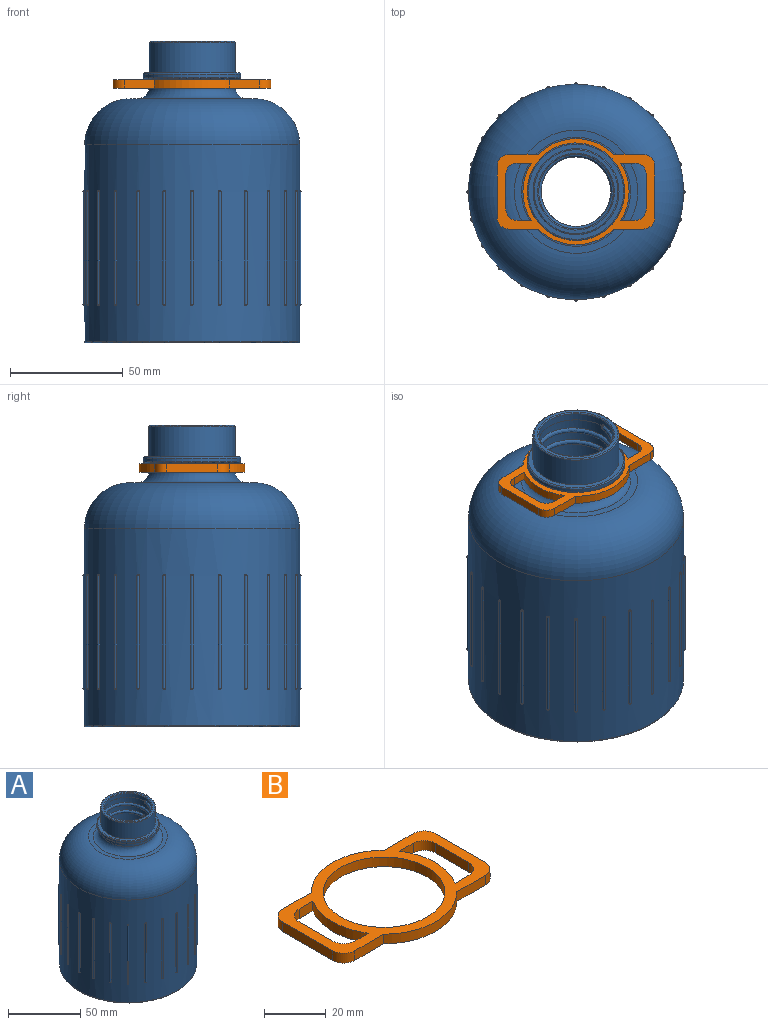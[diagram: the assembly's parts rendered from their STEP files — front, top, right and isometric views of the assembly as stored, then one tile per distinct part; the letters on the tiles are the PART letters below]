
ASSEMBLY  parts=2 mates=1
PART A: 166 faces, bbox 103.6x109.9x133.9 mm
  f0: cylinder r=47.62mm len=95.25mm, axis (0,0,1), area 24527mm2, adj f13,f29,f46,f47,f48,f49,f50,f51
  f1: cylinder r=16.51mm len=33.02mm, axis (0,0,1), area 332.1mm2, adj f3,f38,f39,f40,f43
  f2: cylinder r=16.52mm len=33.05mm, axis (0,0,1), area 865.6mm2, adj f3,f36,f37,f38,f39,f40,f41
  f3: plane 33.05x33.05mm, normal (0,0,-1), area 1.1mm2, adj f1,f2,f38,f39
  f4: cylinder r=16.51mm len=33.02mm, axis (0,0,1), area 780mm2, adj f31,f36,f37,f39,f41
  f5: plane 87.63x87.63mm, normal (0,0,1), area 679mm2, adj f10,f32
  f6: cylinder r=19.05mm len=38.1mm, axis (0,0,-1), area 456mm2, adj f30,f35
  f7: cylinder r=45.09mm len=90.17mm, axis (0,0,-1), area 945.5mm2, adj f8,f23,f25,f26,f28
  f8: plane 90.17x90.17mm, normal (0,0,-1), area 2.8mm2, adj f7,f22,f23,f25
  f9: plane 83.82x83.82mm, normal (0,0,-1), area 165.9mm2, adj f10,f18
  f10: cylinder r=41.27mm len=82.55mm, axis (0,0,1), area 16964.1mm2, adj f5,f9
  f11: plane 94.23x94.23mm, normal (0,0,-1), area 443.9mm2, adj f28,f29
  f12: plane 54.61x54.61mm, normal (0,0,1), area 513mm2, adj f13,f30
  f13: torus R=27.3mm, axis (0,0,1), area 8070.4mm2, adj f0,f12
  f14: cylinder r=19.05mm len=38.1mm, axis (0,0,-1), area 1611.3mm2, adj f34,f42
  f15: plane 37.08x37.08mm, normal (0,0,1), area 170.3mm2, adj f42,f43
  f16: plane 90.17x90.17mm, normal (0,0,-1), area 178.6mm2, adj f17,f19
  f17: cylinder r=45.09mm len=90.17mm, axis (0,0,-1), area 1089.4mm2, adj f16,f21,f24,f25,f27
  f18: cylinder r=41.91mm len=83.82mm, axis (0,0,-1), area 535.1mm2, adj f9,f20
  f19: cylinder r=44.45mm len=88.9mm, axis (0,0,-1), area 567.5mm2, adj f16,f20
  f20: plane 88.9x88.9mm, normal (0,0,-1), area 689.1mm2, adj f18,f19
  f21: plane 90.17x90.17mm, normal (0,0,1), area 2.8mm2, adj f17,f22,f24,f25
  f22: cylinder r=45.07mm len=90.14mm, axis (0,0,-1), area 1347.5mm2, adj f8,f21,f23,f24,f25,f26,f27
  f23: plane 0.25x0.14mm, normal (0,1,0), area 0mm2, adj f7,f8,f22,f26
  f24: plane 0.25x0.14mm, normal (0,1,0), area 0mm2, adj f17,f21,f22,f27
  f25: bspline ~109.4x94.74mm, area 1485mm2, adj f7,f8,f17,f21,f22,f26,f27
  f26: bspline ~2.31x1.44mm, area 3.9mm2, adj f7,f22,f23,f25
  f27: bspline ~2.31x1.44mm, area 3.9mm2, adj f17,f22,f24,f25
  f28: torus R=45.59mm, axis (0,0,1), area 227mm2, adj f7,f11
  f29: torus R=47.12mm, axis (0,0,1), area 237.9mm2, adj f0,f11
  f30: torus R=24.13mm, axis (0,0,1), area 1047.7mm2, adj f6,f12
  f31: torus R=21.59mm, axis (0,0,-1), area 904.7mm2, adj f4,f32
  f32: torus R=20.96mm, axis (0,0,1), area 7942.1mm2, adj f5,f31
  f33: cylinder r=21.59mm len=43.18mm, axis (0,0,-1), area 206.7mm2, adj f44,f45
  f34: plane 42.16x42.16mm, normal (0,0,1), area 256.2mm2, adj f14,f45
  f35: plane 42.16x42.16mm, normal (0,0,-1), area 256.2mm2, adj f6,f44
  f36: plane 33.05x33.05mm, normal (0,0,1), area 1.1mm2, adj f2,f4,f37,f39
  f37: plane 0.25x0.17mm, normal (0,-1,0), area 0mm2, adj f2,f4,f36,f41
  f38: plane 0.25x0.17mm, normal (0,1,0), area 0mm2, adj f1,f2,f3,f40
  f39: bspline ~33.04x33.01mm, area 710.9mm2, adj f1,f2,f3,f4,f36,f40,f41
  f40: bspline ~2.35x1.67mm, area 4mm2, adj f1,f2,f38,f39
  f41: bspline ~2.35x1.67mm, area 4mm2, adj f2,f4,f37,f39
  f42: torus R=18.54mm, axis (0,0,1), area 94.6mm2, adj f14,f15
  f43: torus R=17.02mm, axis (0,0,1), area 83.7mm2, adj f1,f15
  f44: torus R=21.08mm, axis (0,0,1), area 107.3mm2, adj f33,f35
  f45: torus R=21.08mm, axis (0,0,1), area 107.3mm2, adj f33,f34
  f46: cylinder r=0.64mm len=49.78mm, axis (0,0,-1), area 99.7mm2, adj f0,f141,f165
  f47: plane 0.25x0.13mm, normal (0,0,1), area 0mm2, adj f0,f165
  f48: plane 0.25x0.13mm, normal (0,0,-1), area 0mm2, adj f0,f141
  f49: cylinder r=0.64mm len=49.78mm, axis (0,0,-1), area 99.7mm2, adj f0,f140,f164
  f50: plane 0.25x0.16mm, normal (0,0,1), area 0mm2, adj f0,f164
  f51: plane 0.25x0.16mm, normal (0,0,-1), area 0mm2, adj f0,f140
  f52: cylinder r=0.64mm len=49.78mm, axis (0,0,-1), area 99.7mm2, adj f0,f139,f163
  f53: plane 0.24x0.19mm, normal (0,0,1), area 0mm2, adj f0,f163
  f54: plane 0.24x0.19mm, normal (0,0,-1), area 0mm2, adj f0,f139
  f55: cylinder r=0.64mm len=49.78mm, axis (0,0,-1), area 99.7mm2, adj f0,f138,f162
  f56: plane 0.22x0.22mm, normal (0,0,1), area 0mm2, adj f0,f162
  f57: plane 0.22x0.22mm, normal (0,0,-1), area 0mm2, adj f0,f138
  f58: cylinder r=0.64mm len=49.78mm, axis (0,0,-1), area 99.7mm2, adj f0,f137,f161
  f59: plane 0.24x0.19mm, normal (0,0,1), area 0mm2, adj f0,f161
  f60: plane 0.24x0.19mm, normal (0,0,-1), area 0mm2, adj f0,f137
  f61: cylinder r=0.64mm len=49.78mm, axis (0,0,-1), area 99.7mm2, adj f0,f136,f160
  f62: plane 0.25x0.16mm, normal (0,0,1), area 0mm2, adj f0,f160
  f63: plane 0.25x0.16mm, normal (0,0,-1), area 0mm2, adj f0,f136
  f64: cylinder r=0.64mm len=49.78mm, axis (0,0,-1), area 99.7mm2, adj f0,f135,f159
  f65: plane 0.25x0.13mm, normal (0,0,1), area 0mm2, adj f0,f159
  f66: plane 0.76x0.64mm, normal (0,0,-1), area 0mm2, adj f0,f135
  f67: cylinder r=0.64mm len=49.78mm, axis (0,0,-1), area 99.7mm2, adj f0,f134,f158
  f68: plane 0.25x0.16mm, normal (0,0,1), area 0mm2, adj f0,f158
  f69: plane 0.25x0.16mm, normal (0,0,-1), area 0mm2, adj f0,f134
  f70: cylinder r=0.64mm len=49.78mm, axis (0,0,-1), area 99.7mm2, adj f0,f133,f157
  f71: plane 0.24x0.19mm, normal (0,0,1), area 0mm2, adj f0,f157
  f72: plane 0.24x0.19mm, normal (0,0,-1), area 0mm2, adj f0,f133
  f73: cylinder r=0.64mm len=49.78mm, axis (0,0,-1), area 99.7mm2, adj f0,f132,f156
  f74: plane 0.22x0.22mm, normal (0,0,1), area 0mm2, adj f0,f156
  f75: plane 0.22x0.22mm, normal (0,0,-1), area 0mm2, adj f0,f132
  f76: cylinder r=0.64mm len=49.78mm, axis (0,0,-1), area 99.7mm2, adj f0,f131,f155
  f77: plane 0.24x0.19mm, normal (0,0,1), area 0mm2, adj f0,f155
  f78: plane 0.24x0.19mm, normal (0,0,-1), area 0mm2, adj f0,f131
  f79: cylinder r=0.64mm len=49.78mm, axis (0,0,-1), area 99.7mm2, adj f0,f130,f154
  f80: plane 0.25x0.16mm, normal (0,0,1), area 0mm2, adj f0,f154
  f81: plane 0.25x0.16mm, normal (0,0,-1), area 0mm2, adj f0,f130
  f82: cylinder r=0.64mm len=49.78mm, axis (0,0,-1), area 99.7mm2, adj f0,f129,f153
  f83: plane 0.25x0.13mm, normal (0,0,1), area 0mm2, adj f0,f153
  f84: plane 0.25x0.13mm, normal (0,0,-1), area 0mm2, adj f0,f129
  f85: cylinder r=0.64mm len=49.78mm, axis (0,0,-1), area 99.7mm2, adj f0,f128,f152
  f86: plane 0.25x0.16mm, normal (0,0,1), area 0mm2, adj f0,f152
  f87: plane 0.25x0.16mm, normal (0,0,-1), area 0mm2, adj f0,f128
  f88: cylinder r=0.64mm len=49.78mm, axis (0,0,-1), area 99.7mm2, adj f0,f127,f151
  f89: plane 0.24x0.19mm, normal (0,0,1), area 0mm2, adj f0,f151
  f90: plane 0.24x0.19mm, normal (0,0,-1), area 0mm2, adj f0,f127
  f91: cylinder r=0.64mm len=49.78mm, axis (0,0,-1), area 99.7mm2, adj f0,f126,f150
  f92: plane 0.22x0.22mm, normal (0,0,1), area 0mm2, adj f0,f150
  f93: plane 0.22x0.22mm, normal (0,0,-1), area 0mm2, adj f0,f126
  f94: cylinder r=0.64mm len=49.78mm, axis (0,0,-1), area 99.7mm2, adj f0,f125,f149
  f95: plane 0.24x0.19mm, normal (0,0,1), area 0mm2, adj f0,f149
  f96: plane 0.24x0.19mm, normal (0,0,-1), area 0mm2, adj f0,f125
  f97: cylinder r=0.64mm len=49.78mm, axis (0,0,-1), area 99.7mm2, adj f0,f124,f148
  f98: plane 0.25x0.16mm, normal (0,0,1), area 0mm2, adj f0,f148
  f99: plane 0.25x0.16mm, normal (0,0,-1), area 0mm2, adj f0,f124
  f100: cylinder r=0.64mm len=49.78mm, axis (0,0,-1), area 99.7mm2, adj f0,f123,f147
  f101: plane 0.25x0.13mm, normal (0,0,1), area 0mm2, adj f0,f147
  f102: plane 0.76x0.64mm, normal (0,0,-1), area 0mm2, adj f0,f123
  f103: cylinder r=0.64mm len=49.78mm, axis (0,0,-1), area 99.7mm2, adj f0,f122,f146
  f104: plane 0.25x0.16mm, normal (0,0,1), area 0mm2, adj f0,f146
  f105: plane 0.25x0.16mm, normal (0,0,-1), area 0mm2, adj f0,f122
  f106: cylinder r=0.64mm len=49.78mm, axis (0,0,-1), area 99.7mm2, adj f0,f121,f145
  f107: plane 0.24x0.19mm, normal (0,0,1), area 0mm2, adj f0,f145
  f108: plane 0.24x0.19mm, normal (0,0,-1), area 0mm2, adj f0,f121
  f109: cylinder r=0.64mm len=49.78mm, axis (0,0,-1), area 99.7mm2, adj f0,f120,f144
  f110: plane 0.22x0.22mm, normal (0,0,1), area 0mm2, adj f0,f144
  f111: plane 0.22x0.22mm, normal (0,0,-1), area 0mm2, adj f0,f120
  f112: cylinder r=0.64mm len=49.78mm, axis (0,0,-1), area 99.7mm2, adj f0,f119,f143
  f113: plane 0.24x0.19mm, normal (0,0,1), area 0mm2, adj f0,f143
  f114: plane 0.24x0.19mm, normal (0,0,-1), area 0mm2, adj f0,f119
  f115: cylinder r=0.64mm len=49.78mm, axis (0,0,-1), area 99.7mm2, adj f0,f118,f142
  f116: plane 0.25x0.16mm, normal (0,0,1), area 0mm2, adj f0,f142
  f117: plane 0.25x0.16mm, normal (0,0,-1), area 0mm2, adj f0,f118
  f118: torus R=0.13mm, axis (0,0,-1), area 1.1mm2, adj f0,f115,f117
  f119: torus R=0.13mm, axis (0,0,-1), area 1.1mm2, adj f0,f112,f114
  f120: torus R=0.13mm, axis (0,0,-1), area 1.1mm2, adj f0,f109,f111
  f121: torus R=0.13mm, axis (0,0,-1), area 1.1mm2, adj f0,f106,f108
  f122: torus R=0.13mm, axis (0,0,-1), area 1.1mm2, adj f0,f103,f105
  f123: torus R=0.13mm, axis (0,0,-1), area 1.6mm2, adj f0,f100,f102
  f124: torus R=0.13mm, axis (0,0,-1), area 1.1mm2, adj f0,f97,f99
  f125: torus R=0.13mm, axis (0,0,-1), area 1.1mm2, adj f0,f94,f96
  f126: torus R=0.13mm, axis (0,0,-1), area 1.1mm2, adj f0,f91,f93
  f127: torus R=0.13mm, axis (0,0,-1), area 1.1mm2, adj f0,f88,f90
  f128: torus R=0.13mm, axis (0,0,-1), area 1.1mm2, adj f0,f85,f87
  f129: torus R=0.13mm, axis (0,0,-1), area 1.1mm2, adj f0,f82,f84
  f130: torus R=0.13mm, axis (0,0,-1), area 1.1mm2, adj f0,f79,f81
  f131: torus R=0.13mm, axis (0,0,-1), area 1.1mm2, adj f0,f76,f78
  f132: torus R=0.13mm, axis (0,0,-1), area 1.1mm2, adj f0,f73,f75
  f133: torus R=0.13mm, axis (0,0,-1), area 1.1mm2, adj f0,f70,f72
  f134: torus R=0.13mm, axis (0,0,-1), area 1.1mm2, adj f0,f67,f69
  f135: torus R=0.13mm, axis (0,0,-1), area 0.7mm2, adj f0,f64,f66
  f136: torus R=0.13mm, axis (0,0,-1), area 1.1mm2, adj f0,f61,f63
  f137: torus R=0.13mm, axis (0,0,-1), area 1.1mm2, adj f0,f58,f60
  f138: torus R=0.13mm, axis (0,0,-1), area 1.1mm2, adj f0,f55,f57
  f139: torus R=0.13mm, axis (0,0,-1), area 1.1mm2, adj f0,f52,f54
  f140: torus R=0.13mm, axis (0,0,-1), area 1.1mm2, adj f0,f49,f51
  f141: torus R=0.13mm, axis (0,0,-1), area 1.1mm2, adj f0,f46,f48
  f142: torus R=0.13mm, axis (0,0,-1), area 1.1mm2, adj f0,f115,f116
  f143: torus R=0.13mm, axis (0,0,-1), area 1.1mm2, adj f0,f112,f113
  f144: torus R=0.13mm, axis (0,0,-1), area 1.1mm2, adj f0,f109,f110
  f145: torus R=0.13mm, axis (0,0,-1), area 1.1mm2, adj f0,f106,f107
  f146: torus R=0.13mm, axis (0,0,-1), area 1.1mm2, adj f0,f103,f104
  f147: torus R=0.13mm, axis (0,0,-1), area 1.1mm2, adj f0,f100,f101
  f148: torus R=0.13mm, axis (0,0,-1), area 1.1mm2, adj f0,f97,f98
  f149: torus R=0.13mm, axis (0,0,-1), area 1.1mm2, adj f0,f94,f95
  f150: torus R=0.13mm, axis (0,0,-1), area 1.1mm2, adj f0,f91,f92
  f151: torus R=0.13mm, axis (0,0,-1), area 1.1mm2, adj f0,f88,f89
  f152: torus R=0.13mm, axis (0,0,-1), area 1.1mm2, adj f0,f85,f86
  f153: torus R=0.13mm, axis (0,0,-1), area 1.1mm2, adj f0,f82,f83
  f154: torus R=0.13mm, axis (0,0,-1), area 1.1mm2, adj f0,f79,f80
  f155: torus R=0.13mm, axis (0,0,-1), area 1.1mm2, adj f0,f76,f77
  f156: torus R=0.13mm, axis (0,0,-1), area 1.1mm2, adj f0,f73,f74
  f157: torus R=0.13mm, axis (0,0,-1), area 1.1mm2, adj f0,f70,f71
  f158: torus R=0.13mm, axis (0,0,-1), area 1.1mm2, adj f0,f67,f68
  f159: torus R=0.13mm, axis (0,0,-1), area 1.1mm2, adj f0,f64,f65
  f160: torus R=0.13mm, axis (0,0,-1), area 1.1mm2, adj f0,f61,f62
  f161: torus R=0.13mm, axis (0,0,-1), area 1.1mm2, adj f0,f58,f59
  f162: torus R=0.13mm, axis (0,0,-1), area 1.1mm2, adj f0,f55,f56
  f163: torus R=0.13mm, axis (0,0,-1), area 1.1mm2, adj f0,f52,f53
  f164: torus R=0.13mm, axis (0,0,-1), area 1.1mm2, adj f0,f49,f50
  f165: torus R=0.13mm, axis (0,0,-1), area 1.1mm2, adj f0,f46,f47
PART B: 27 faces, bbox 69.9x47x3.8 mm
  f0: plane 13.13x3.81mm, normal (0,-1,0), area 50mm2, adj f13,f17,f18,f23
  f1: plane 22.86x3.81mm, normal (1,0,0), area 87.1mm2, adj f17,f18,f23,f24
  f2: plane 13.13x3.81mm, normal (0,1,0), area 50mm2, adj f3,f17,f18,f24
  f3: cylinder r=23.49mm len=33.43mm, axis (0,0,-1), area 141.7mm2, adj f2,f4,f17,f18
  f4: plane 13.13x3.81mm, normal (0,1,0), area 50mm2, adj f3,f17,f18,f25
  f5: plane 22.86x3.81mm, normal (-1,0,0), area 87.1mm2, adj f17,f18,f25,f26
  f6: plane 13.13x3.81mm, normal (0,-1,0), area 50mm2, adj f13,f17,f18,f26
  f7: plane 15.24x3.81mm, normal (-1,0,0), area 58.1mm2, adj f17,f18,f21,f22
  f8: plane 6.27x3.81mm, normal (0,1,0), area 23.9mm2, adj f9,f17,f18,f21
  f9: cylinder r=23.49mm len=25.4mm, axis (0,0,-1), area 102.2mm2, adj f8,f14,f17,f18
  f10: plane 6.27x3.81mm, normal (0,-1,0), area 23.9mm2, adj f11,f17,f18,f20
  f11: cylinder r=23.49mm len=25.4mm, axis (0,0,-1), area 102.2mm2, adj f10,f12,f17,f18
  f12: plane 6.27x3.81mm, normal (0,1,0), area 23.9mm2, adj f11,f17,f18,f19
  f13: cylinder r=23.49mm len=33.43mm, axis (0,0,-1), area 141.7mm2, adj f0,f6,f17,f18
  f14: plane 6.27x3.81mm, normal (0,-1,0), area 23.9mm2, adj f9,f17,f18,f22
  f15: plane 15.24x3.81mm, normal (1,0,0), area 58.1mm2, adj f17,f18,f19,f20
  f16: cylinder r=19.69mm len=39.37mm, axis (0,0,-1), area 471.2mm2, adj f17,f18
  f17: plane 69.85x46.99mm, normal (0,0,1), area 963mm2, adj f0,f1,f2,f3,f4,f5,f6,f7
  f18: plane 69.85x46.99mm, normal (0,0,-1), area 963mm2, adj f0,f1,f2,f3,f4,f5,f6,f7
  f19: cylinder r=5.08mm len=5.08mm, axis (0,0,1), area 30.4mm2, adj f12,f15,f17,f18
  f20: cylinder r=5.08mm len=5.08mm, axis (0,0,-1), area 30.4mm2, adj f10,f15,f17,f18
  f21: cylinder r=5.08mm len=5.08mm, axis (0,0,-1), area 30.4mm2, adj f7,f8,f17,f18
  f22: cylinder r=5.08mm len=5.08mm, axis (0,0,1), area 30.4mm2, adj f7,f14,f17,f18
  f23: cylinder r=5.08mm len=5.08mm, axis (0,0,1), area 30.4mm2, adj f0,f1,f17,f18
  f24: cylinder r=5.08mm len=5.08mm, axis (0,0,-1), area 30.4mm2, adj f1,f2,f17,f18
  f25: cylinder r=5.08mm len=5.08mm, axis (0,0,1), area 30.4mm2, adj f4,f5,f17,f18
  f26: cylinder r=5.08mm len=5.08mm, axis (0,0,-1), area 30.4mm2, adj f5,f6,f17,f18
PLACE A t=(126.23,-0.47,-13.97)mm
PLACE B t=(1.32,-0.47,-2.93)mm
MATE cylindrical A.f6 <-> B.f9  axis (0,0,-1) through (126.23,-0.47,3.81)mm
